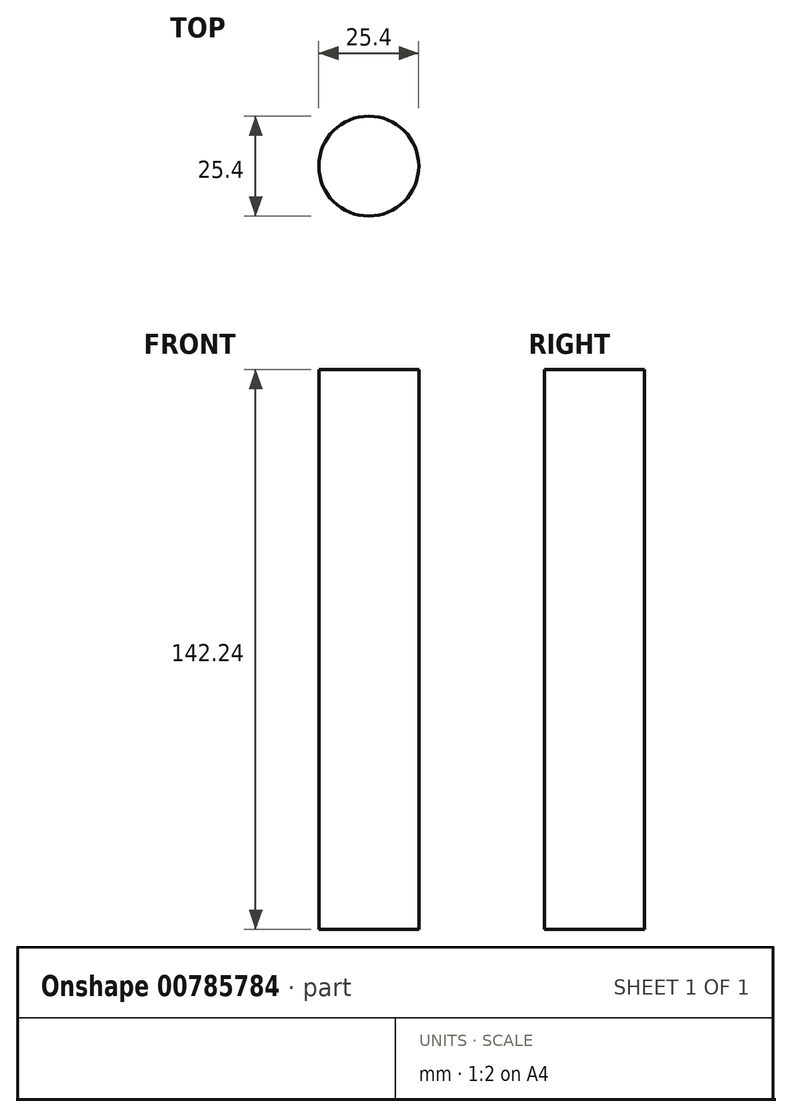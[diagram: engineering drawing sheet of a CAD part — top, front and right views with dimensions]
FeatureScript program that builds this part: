
annotation { "Feature Type Name" : "Feature", "Feature Type Description" : "" }
export const myFeature = defineFeature(function(context is Context, id is Id, definition is map)
    precondition{}
    {
        {
            var Q0;
            Q0=qCreatedBy(makeId("Top.planeOp"),FACE);
            var sketch = newSketch(context, id + "F0", { "sketchPlane" : qUnion([Q0])});
            skCircle(sketch, "E0", {"center": v(-51.92, -44.16) * mm, "radius": 12.7 * mm});
            skSolve(sketch);
        }
        {
            var Q0;
            Q0=makeQuery(id+"F0.imprint","IMPRINT",FACE,{"disambiguationData":[TD([[makeQuery(id+"F0.imprint","IMPRINT",EDGE,{"derivedFrom":sQuery(id+"F0.wireOp",EDGE,"E0")}),1.0]])]});
            var Q1;
            Q1=sQuery(id+"F0.wireOp",EDGE,"E0");
            extrude(context, id + "F1", {"entities" : qUnion([Q0]), "surfaceEntities" : qUnion([Q1]), "depth" : 142.24 * mm, "offsetDistance" : 25.4 * mm});
        }
    });
